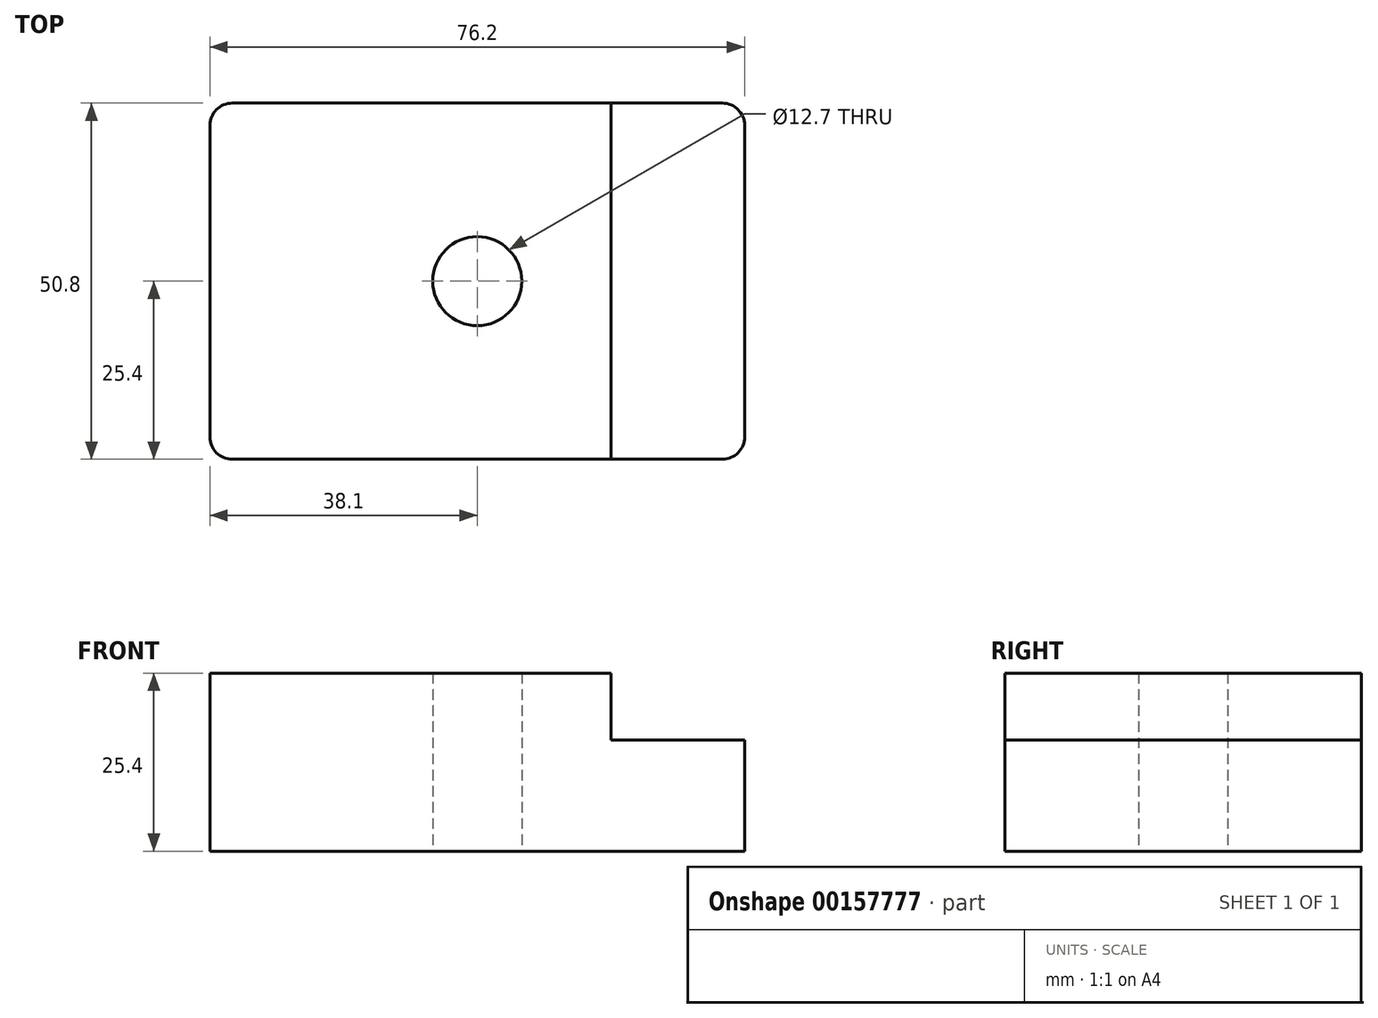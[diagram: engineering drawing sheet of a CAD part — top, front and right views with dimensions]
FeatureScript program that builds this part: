
annotation { "Feature Type Name" : "Feature", "Feature Type Description" : "" }
export const myFeature = defineFeature(function(context is Context, id is Id, definition is map)
    precondition{}
    {
        {
            var Q0;
            Q0=qCreatedBy(makeId("Top.planeOp"),FACE);
            var sketch = newSketch(context, id + "F0", { "sketchPlane" : qUnion([Q0])});
            skLineSegment(sketch, "E0.bottom", {"start": v(34.93, -25.4) * mm, "end": v(-34.93, -25.4) * mm});
            skLineSegment(sketch, "E0.top", {"start": v(34.93, 25.4) * mm, "end": v(-34.93, 25.4) * mm});
            skLineSegment(sketch, "E0.left", {"start": v(38.1, -22.22) * mm, "end": v(38.1, 22.23) * mm});
            skLineSegment(sketch, "E0.right", {"start": v(-38.1, -22.23) * mm, "end": v(-38.1, 22.22) * mm});
            skPoint(sketch, "E0.middle", {"position": v(0, 0) * mm});
            skPoint(sketch, "E1.visualSharp", {"position": v(-38.1, 25.4) * mm});
            skArc(sketch, "E1.filletArc", {"start": v(-34.93, 25.4) * mm, "mid": v(-37.17, 24.47) * mm, "end": v(-38.1, 22.22) * mm});
            skPoint(sketch, "E2.visualSharp", {"position": v(-38.1, -25.4) * mm});
            skArc(sketch, "E2.filletArc", {"start": v(-38.1, -22.23) * mm, "mid": v(-37.17, -24.47) * mm, "end": v(-34.93, -25.4) * mm});
            skPoint(sketch, "E3.visualSharp", {"position": v(38.1, -25.4) * mm});
            skArc(sketch, "E3.filletArc", {"start": v(34.93, -25.4) * mm, "mid": v(37.17, -24.47) * mm, "end": v(38.1, -22.22) * mm});
            skPoint(sketch, "E4.visualSharp", {"position": v(38.1, 25.4) * mm});
            skArc(sketch, "E4.filletArc", {"start": v(38.1, 22.23) * mm, "mid": v(37.17, 24.47) * mm, "end": v(34.93, 25.4) * mm});
            skCircle(sketch, "E5", {"center": v(0, 0) * mm, "radius": 6.35 * mm});
            skSolve(sketch);
        }
        {
            var Q0;
            Q0 = qSketchRegion(id + "F0", true);
            extrude(context, id + "F1", {"entities" : qUnion([Q0]), "depth" : 25.4 * mm});
        }
        {
            var Q0;
            Q0=qCreatedBy(makeId("Front.planeOp"),FACE);
            var sketch = newSketch(context, id + "F2", { "sketchPlane" : qUnion([Q0])});
            skLineSegment(sketch, "E6.bottom", {"start": v(19.05, 25.4) * mm, "end": v(38.1, 25.4) * mm});
            skLineSegment(sketch, "E6.top", {"start": v(19.05, 15.88) * mm, "end": v(38.1, 15.88) * mm});
            skLineSegment(sketch, "E6.left", {"start": v(19.05, 25.4) * mm, "end": v(19.05, 15.88) * mm});
            skLineSegment(sketch, "E6.right", {"start": v(38.1, 25.4) * mm, "end": v(38.1, 15.88) * mm});
            skSolve(sketch);
        }
        {
            var Q0;
            Q0 = qSketchRegion(id + "F2", true);
            extrude(context, id + "F3", {"entities" : qUnion([Q0]), "operationType" : NewBodyOperationType.REMOVE, "endBound" : BoundingType.THROUGH_ALL, "depth" : 25.4 * mm, "hasSecondDirection" : true, "secondDirectionBound" : SecondDirectionBoundingType.THROUGH_ALL, "secondDirectionOppositeDirection" : true, "secondDirectionDepth" : 25.4 * mm});
        }
    });
